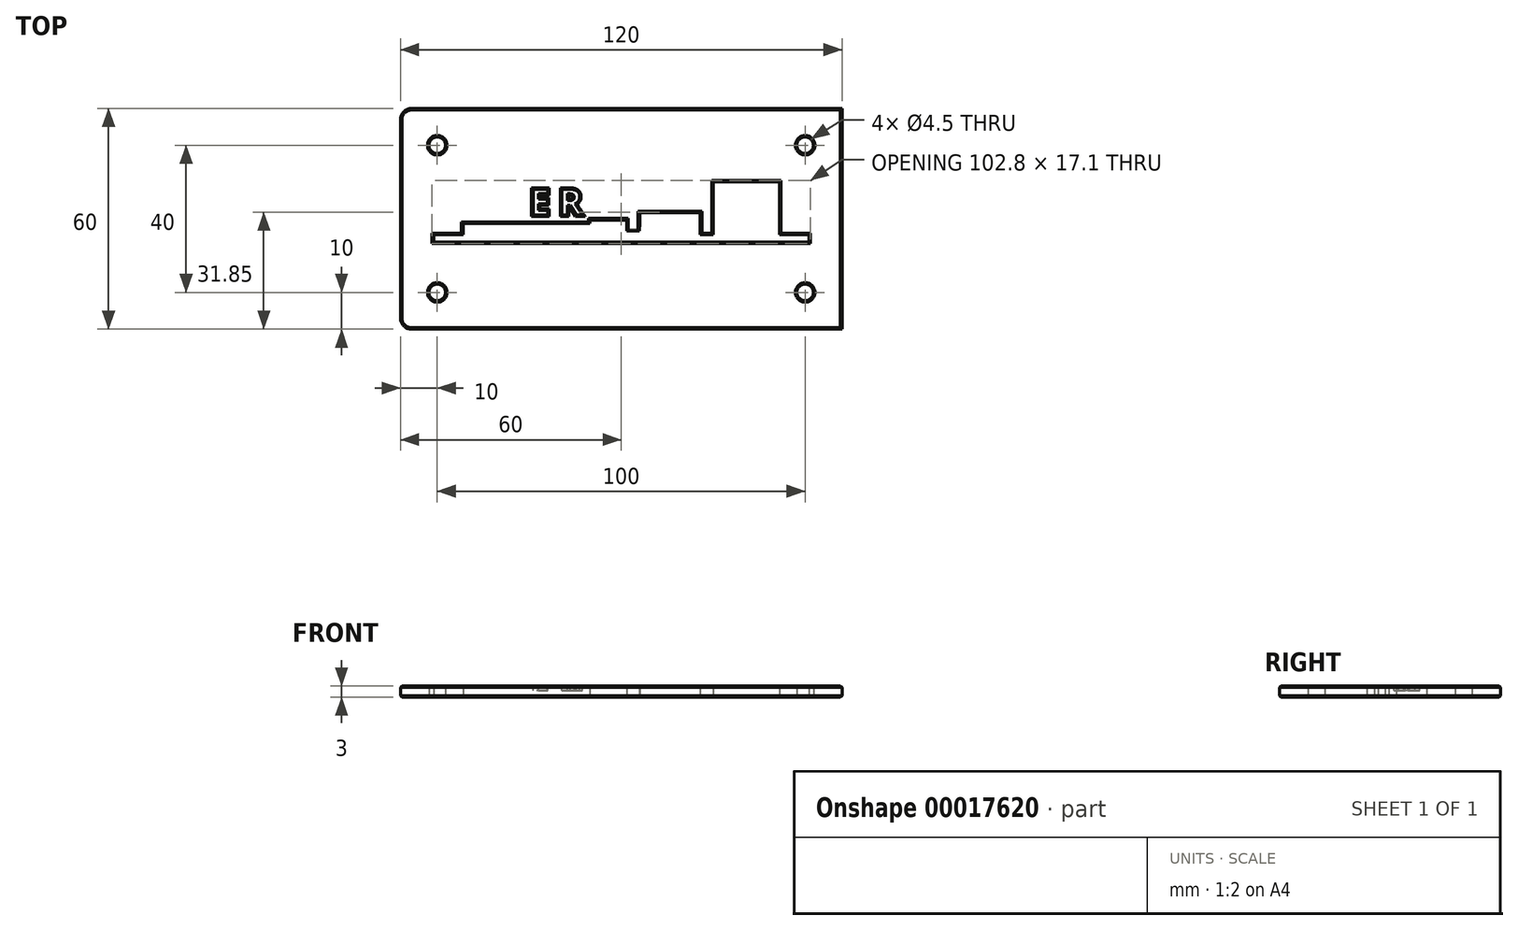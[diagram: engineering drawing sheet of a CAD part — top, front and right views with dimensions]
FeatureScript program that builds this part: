
annotation { "Feature Type Name" : "Feature", "Feature Type Description" : "" }
export const myFeature = defineFeature(function(context is Context, id is Id, definition is map)
    precondition{}
    {
        {
            var Q0;
            Q0=qCreatedBy(makeId("Top.planeOp"),FACE);
            var sketch = newSketch(context, id + "F0", { "sketchPlane" : qUnion([Q0])});
            skLineSegment(sketch, "E0.rect.bottom", {"start": v(-52.5, -30) * mm, "end": v(60, -30) * mm});
            skLineSegment(sketch, "E0.rect.top", {"start": v(-55, 30) * mm, "end": v(60, 30) * mm});
            skLineSegment(sketch, "E0.rect.left", {"start": v(-60, -22.5) * mm, "end": v(-60, 20) * mm});
            skLineSegment(sketch, "E0.rect.right", {"start": v(60, -30) * mm, "end": v(60, 30) * mm});
            skPoint(sketch, "E0.rect.middle", {"position": v(0, 0) * mm});
            skLineSegment(sketch, "E1.left", {"start": v(-60, -30) * mm, "end": v(-60, -22.5) * mm});
            skLineSegment(sketch, "E2.bottom", {"start": v(-60, 30) * mm, "end": v(-55, 30) * mm});
            skLineSegment(sketch, "E2.left", {"start": v(-60, 30) * mm, "end": v(-60, 20) * mm});
            skLineSegment(sketch, "E3.bottom", {"start": v(60, 30) * mm, "end": v(50, 30) * mm});
            skLineSegment(sketch, "E3.left", {"start": v(60, 30) * mm, "end": v(60, 22.5) * mm});
            skLineSegment(sketch, "E4.bottom", {"start": v(60, -30) * mm, "end": v(55, -30) * mm});
            skLineSegment(sketch, "E4.left", {"start": v(60, -30) * mm, "end": v(60, -22.5) * mm});
            skCircle(sketch, "E5", {"center": v(-50, -20) * mm, "radius": 2.25 * mm});
            skCircle(sketch, "E6", {"center": v(-50, 20) * mm, "radius": 2.25 * mm});
            skCircle(sketch, "E7", {"center": v(50, 20) * mm, "radius": 2.25 * mm});
            skCircle(sketch, "E8", {"center": v(50, -20) * mm, "radius": 2.25 * mm});
            skLineSegment(sketch, "E9", {"start": v(-51, 6.3) * mm, "end": v(1.5, 6.3) * mm});
            skLineSegment(sketch, "E10.top", {"start": v(-51, 4.3) * mm, "end": v(-43, 4.3) * mm});
            skLineSegment(sketch, "E10.left", {"start": v(-51, 6.3) * mm, "end": v(-51, 4.3) * mm});
            skLineSegment(sketch, "E10.right", {"start": v(51, 6.3) * mm, "end": v(51, 4.3) * mm});
            skLineSegment(sketch, "E11.top", {"start": v(-43, 1.3) * mm, "end": v(-8.5, 1.3) * mm});
            skLineSegment(sketch, "E11.left", {"start": v(-43, 4.3) * mm, "end": v(-43, 1.3) * mm});
            skLineSegment(sketch, "E11.right", {"start": v(43, 4.3) * mm, "end": v(43, 1.3) * mm});
            skLineSegment(sketch, "E12.trimOffspring", {"start": v(43, 4.3) * mm, "end": v(51, 4.3) * mm});
            skLineSegment(sketch, "E13.right", {"start": v(-8.5, 1.3) * mm, "end": v(-8.5, 0.3) * mm});
            skLineSegment(sketch, "E14.left", {"start": v(-8.5, 0.3) * mm, "end": v(-8.5, 1.3) * mm});
            skLineSegment(sketch, "E14.right", {"start": v(1.5, 0.3) * mm, "end": v(1.5, 1.3) * mm});
            skLineSegment(sketch, "E15.top", {"start": v(43, -10) * mm, "end": v(25, -10) * mm});
            skLineSegment(sketch, "E15.left", {"start": v(43, 1.3) * mm, "end": v(43, -10) * mm});
            skLineSegment(sketch, "E15.right", {"start": v(25, 1.3) * mm, "end": v(25, -10) * mm});
            skLineSegment(sketch, "E16.top", {"start": v(-8.5, 0.3) * mm, "end": v(1.5, 0.3) * mm});
            skLineSegment(sketch, "E16.right", {"start": v(1.5, 1.3) * mm, "end": v(1.5, 0.3) * mm});
            skLineSegment(sketch, "E17", {"start": v(-60, -30) * mm, "end": v(-52.5, -30) * mm});
            skLineSegment(sketch, "E18.left", {"start": v(25, 1.3) * mm, "end": v(25, 4.3) * mm});
            skLineSegment(sketch, "E18.right", {"start": v(21.5, 1.3) * mm, "end": v(21.5, 4.3) * mm});
            skLineSegment(sketch, "E19.left", {"start": v(1.5, 1.3) * mm, "end": v(1.5, 3.3) * mm});
            skLineSegment(sketch, "E20.top", {"start": v(5, -1.7) * mm, "end": v(21.5, -1.7) * mm});
            skLineSegment(sketch, "E20.left", {"start": v(5, 1.3) * mm, "end": v(5, -1.7) * mm});
            skLineSegment(sketch, "E20.right", {"start": v(21.5, 1.3) * mm, "end": v(21.5, -1.7) * mm});
            skLineSegment(sketch, "E21.trimOffspring", {"start": v(5, 6.3) * mm, "end": v(21.5, 6.3) * mm});
            skLineSegment(sketch, "E22.trimOffspring", {"start": v(25, 6.3) * mm, "end": v(51, 6.3) * mm});
            skLineSegment(sketch, "E23", {"start": v(-43, 4.3) * mm, "end": v(5, 4.3) * mm, "construction": true});
            skLineSegment(sketch, "E24", {"start": v(21.5, 4.3) * mm, "end": v(25, 4.3) * mm});
            skLineSegment(sketch, "E25", {"start": v(1.5, 6.3) * mm, "end": v(5, 6.3) * mm});
            skLineSegment(sketch, "E26", {"start": v(21.5, 6.3) * mm, "end": v(25, 6.3) * mm});
            skLineSegment(sketch, "E27", {"start": v(4.98, 3.3) * mm, "end": v(1.5, 3.3) * mm});
            skLineSegment(sketch, "E28.trimOffspring", {"start": v(21.5, 4.3) * mm, "end": v(43, 4.3) * mm, "construction": true});
            skLineSegment(sketch, "E29", {"start": v(4.98, 3.3) * mm, "end": v(5, 1.3) * mm});
            skLineSegment(sketch, "E30", {"start": v(21.5, 4.3) * mm, "end": v(5, 4.3) * mm, "construction": true});
            skSolve(sketch);
        }
        {
            var Q0;
            Q0=makeQuery(id+"F0.imprint","IMPRINT",FACE,{"disambiguationData":[TD([[makeQuery(id+"F0.imprint","IMPRINT",EDGE,{"derivedFrom":sQuery(id+"F0.wireOp",EDGE,"E0.rect.bottom")}),1.0]])]});
            extrude(context, id + "F1", {"entities" : qUnion([Q0]), "oppositeDirection" : true, "depth" : 3 * mm});
        }
        {
            var Q0;
            Q0=makeQuery(id+"F1.opExtrude","SWEPT_EDGE",EDGE,{"disambiguationData":[OSD([sQuery(id+"F0.wireOp",EDGE,"E4.bottom"),sQuery(id+"F0.wireOp",EDGE,"E4.left")])]});
            var Q1;
            Q1=makeQuery(id+"F1.opExtrude","SWEPT_EDGE",EDGE,{"disambiguationData":[OSD([sQuery(id+"F0.wireOp",EDGE,"E1.bottom"),sQuery(id+"F0.wireOp",EDGE,"E1.left")])]});
            var Q2;
            Q2=makeQuery(id+"F1.opExtrude","SWEPT_EDGE",EDGE,{"disambiguationData":[OSD([sQuery(id+"F0.wireOp",EDGE,"E3.bottom"),sQuery(id+"F0.wireOp",EDGE,"E3.left")])]});
            var Q3;
            Q3=makeQuery(id+"F1.opExtrude","SWEPT_EDGE",EDGE,{"disambiguationData":[OSD([sQuery(id+"F0.wireOp",EDGE,"E2.bottom"),sQuery(id+"F0.wireOp",EDGE,"E2.left")])]});
            fillet(context, id + "F2", {"entities" : qUnion([Q0, Q1, Q2, Q3]), "radius" : 3 * mm, "tangentPropagation" : true, "allowEdgeOverflow" : false});
        }
        {
            var Q0;
            Q0=makeQuery(id+"F1.opExtrude","CAP_FACE",FACE,{"disambiguationData":[OSD([sQuery(id+"F0.wireOp",EDGE,"E0.rect.bottom"),sQuery(id+"F0.wireOp",EDGE,"E0.rect.top"),sQuery(id+"F0.wireOp",EDGE,"E0.rect.left"),sQuery(id+"F0.wireOp",EDGE,"E0.rect.right"),sQuery(id+"F0.wireOp",EDGE,"E1.bottom"),sQuery(id+"F0.wireOp",EDGE,"E1.left"),sQuery(id+"F0.wireOp",EDGE,"E2.bottom"),sQuery(id+"F0.wireOp",EDGE,"E2.left"),sQuery(id+"F0.wireOp",EDGE,"E3.bottom"),sQuery(id+"F0.wireOp",EDGE,"E3.left"),sQuery(id+"F0.wireOp",EDGE,"E4.bottom"),sQuery(id+"F0.wireOp",EDGE,"E4.left"),sQuery(id+"F0.wireOp",EDGE,"E5"),sQuery(id+"F0.wireOp",EDGE,"E6"),sQuery(id+"F0.wireOp",EDGE,"E7"),sQuery(id+"F0.wireOp",EDGE,"E8"),sQuery(id+"F0.wireOp",EDGE,"E9"),sQuery(id+"F0.wireOp",EDGE,"E10.top"),sQuery(id+"F0.wireOp",EDGE,"E10.left"),sQuery(id+"F0.wireOp",EDGE,"E10.right"),sQuery(id+"F0.wireOp",EDGE,"E11.left"),sQuery(id+"F0.wireOp",EDGE,"E11.right"),sQuery(id+"F0.wireOp",EDGE,"E12.trimOffspring"),sQuery(id+"F0.wireOp",EDGE,"E11.top"),sQuery(id+"F0.wireOp",EDGE,"E14.bottom"),sQuery(id+"F0.wireOp",EDGE,"E14.left"),sQuery(id+"F0.wireOp",EDGE,"E14.right"),sQuery(id+"F0.wireOp",EDGE,"2bbd994b-3e8e-4b0d-a158-f2154df3f7ed.trimOffspring"),sQuery(id+"F0.wireOp",EDGE,"E15.top"),sQuery(id+"F0.wireOp",EDGE,"E15.left"),sQuery(id+"F0.wireOp",EDGE,"E15.right")])],"isStart":false});
            var sketch = newSketch(context, id + "F3", { "sketchPlane" : qUnion([Q0])});
            skText(sketch, "E31", { "text": "E", "fontName": "OpenSans-Bold.ttf"});
            skText(sketch, "E32", { "text": "R", "fontName": "OpenSans-Bold.ttf"});
            skPoint(sketch, "E33.right.start.orphan", {"position": v(-26.9, 1.1) * mm});
            skPoint(sketch, "E34.orphan", {"position": v(-8.9, -0.9) * mm});
            skPoint(sketch, "E33.bottom.end.orphan", {"position": v(-26.9, -0.9) * mm});
            skPoint(sketch, "E33.bottom.start.orphan", {"position": v(-17.9, -0.9) * mm});
            skLineSegment(sketch, "E35", {"start": v(-43, -1.3) * mm, "end": v(-8.5, -1.3) * mm});
            const initialGuessF3  = {"E31": [-0.02483, 0.0011, 1, 0, 0.007], "E32": [-0.01696, 0.0011, 1, 0, 0.007]};
            skSetInitialGuess(sketch, initialGuessF3);
            skSolve(sketch);
        }
        {
            var Q0;
            Q0=makeQuery(id+"F3.imprint","IMPRINT",FACE,{"disambiguationData":[TD([[makeQuery(id+"F3.imprint","IMPRINT",EDGE,{"derivedFrom":sQuery(id+"F3.wireOp",EDGE,"E31.sketch_text.stroke-0")}),-1.0]])]});
            var Q1;
            Q1=makeQuery(id+"F3.imprint","IMPRINT",FACE,{"disambiguationData":[TD([[makeQuery(id+"F3.imprint","IMPRINT",EDGE,{"derivedFrom":sQuery(id+"F3.wireOp",EDGE,"E32.sketch_text.stroke-0")}),-1.0]])]});
            extrude(context, id + "F4", {"entities" : qUnion([Q0, Q1]), "operationType" : NewBodyOperationType.REMOVE, "oppositeDirection" : true, "depth" : 1.2 * mm});
        }
        {
            var Q0;
            Q0=makeQuery(id+"F4.boolean.opBoolean","COPY",EDGE,{"derivedFrom":makeQuery(id+"F4.opExtrude","CAP_EDGE",EDGE,{"disambiguationData":[OSD([sQuery(id+"F3.wireOp",EDGE,"E31.sketch_text.stroke-1")])],"isStart":true})});
            var Q1;
            Q1=makeQuery(id+"F4.boolean.opBoolean","COPY",EDGE,{"derivedFrom":makeQuery(id+"F4.opExtrude","CAP_EDGE",EDGE,{"disambiguationData":[OSD([sQuery(id+"F3.wireOp",EDGE,"E31.sketch_text.stroke-2")])],"isStart":true})});
            var Q2;
            Q2=makeQuery(id+"F4.boolean.opBoolean","COPY",EDGE,{"derivedFrom":makeQuery(id+"F4.opExtrude","CAP_EDGE",EDGE,{"disambiguationData":[OSD([sQuery(id+"F3.wireOp",EDGE,"E31.sketch_text.stroke-3")])],"isStart":true})});
            var Q3;
            Q3=makeQuery(id+"F4.boolean.opBoolean","COPY",EDGE,{"derivedFrom":makeQuery(id+"F4.opExtrude","CAP_EDGE",EDGE,{"disambiguationData":[OSD([sQuery(id+"F3.wireOp",EDGE,"E31.sketch_text.stroke-4")])],"isStart":true})});
            var Q4;
            Q4=makeQuery(id+"F4.boolean.opBoolean","COPY",EDGE,{"derivedFrom":makeQuery(id+"F4.opExtrude","CAP_EDGE",EDGE,{"disambiguationData":[OSD([sQuery(id+"F3.wireOp",EDGE,"E31.sketch_text.stroke-5")])],"isStart":true})});
            var Q5;
            Q5=makeQuery(id+"F4.boolean.opBoolean","COPY",EDGE,{"derivedFrom":makeQuery(id+"F4.opExtrude","CAP_EDGE",EDGE,{"disambiguationData":[OSD([sQuery(id+"F3.wireOp",EDGE,"E31.sketch_text.stroke-6")])],"isStart":true})});
            var Q6;
            Q6=makeQuery(id+"F4.boolean.opBoolean","COPY",EDGE,{"derivedFrom":makeQuery(id+"F4.opExtrude","CAP_EDGE",EDGE,{"disambiguationData":[OSD([sQuery(id+"F3.wireOp",EDGE,"E31.sketch_text.stroke-7")])],"isStart":true})});
            var Q7;
            Q7=makeQuery(id+"F4.boolean.opBoolean","COPY",EDGE,{"derivedFrom":makeQuery(id+"F4.opExtrude","CAP_EDGE",EDGE,{"disambiguationData":[OSD([sQuery(id+"F3.wireOp",EDGE,"E31.sketch_text.stroke-8")])],"isStart":true})});
            var Q8;
            Q8=makeQuery(id+"F4.boolean.opBoolean","COPY",EDGE,{"derivedFrom":makeQuery(id+"F4.opExtrude","CAP_EDGE",EDGE,{"disambiguationData":[OSD([sQuery(id+"F3.wireOp",EDGE,"E31.sketch_text.stroke-9")])],"isStart":true})});
            var Q9;
            Q9=makeQuery(id+"F4.boolean.opBoolean","COPY",EDGE,{"derivedFrom":makeQuery(id+"F4.opExtrude","CAP_EDGE",EDGE,{"disambiguationData":[OSD([sQuery(id+"F3.wireOp",EDGE,"E31.sketch_text.stroke-10")])],"isStart":true})});
            var Q10;
            Q10=makeQuery(id+"F4.boolean.opBoolean","COPY",EDGE,{"derivedFrom":makeQuery(id+"F4.opExtrude","CAP_EDGE",EDGE,{"disambiguationData":[OSD([sQuery(id+"F3.wireOp",EDGE,"E31.sketch_text.stroke-11")])],"isStart":true})});
            var Q11;
            Q11=makeQuery(id+"F4.boolean.opBoolean","COPY",EDGE,{"derivedFrom":makeQuery(id+"F4.opExtrude","CAP_EDGE",EDGE,{"disambiguationData":[OSD([sQuery(id+"F3.wireOp",EDGE,"E31.sketch_text.stroke-0")])],"isStart":true})});
            var Q12;
            Q12=makeQuery(id+"F4.boolean.opBoolean","COPY",EDGE,{"derivedFrom":makeQuery(id+"F4.opExtrude","CAP_EDGE",EDGE,{"disambiguationData":[OSD([sQuery(id+"F3.wireOp",EDGE,"E32.sketch_text.stroke-9")])],"isStart":true})});
            var Q13;
            Q13=makeQuery(id+"F4.boolean.opBoolean","COPY",EDGE,{"derivedFrom":makeQuery(id+"F4.opExtrude","CAP_EDGE",EDGE,{"disambiguationData":[OSD([sQuery(id+"F3.wireOp",EDGE,"E32.sketch_text.stroke-8")])],"isStart":true})});
            var Q14;
            Q14=makeQuery(id+"F4.boolean.opBoolean","COPY",EDGE,{"derivedFrom":makeQuery(id+"F4.opExtrude","CAP_EDGE",EDGE,{"disambiguationData":[OSD([sQuery(id+"F3.wireOp",EDGE,"E32.sketch_text.stroke-7")])],"isStart":true})});
            var Q15;
            Q15=makeQuery(id+"F4.boolean.opBoolean","COPY",EDGE,{"derivedFrom":makeQuery(id+"F4.opExtrude","CAP_EDGE",EDGE,{"disambiguationData":[OSD([sQuery(id+"F3.wireOp",EDGE,"E32.sketch_text.stroke-18")])],"isStart":true})});
            var Q16;
            Q16=makeQuery(id+"F4.boolean.opBoolean","COPY",EDGE,{"derivedFrom":makeQuery(id+"F4.opExtrude","CAP_EDGE",EDGE,{"disambiguationData":[OSD([sQuery(id+"F3.wireOp",EDGE,"E32.sketch_text.stroke-17")])],"isStart":true})});
            var Q17;
            Q17=makeQuery(id+"F4.boolean.opBoolean","COPY",EDGE,{"derivedFrom":makeQuery(id+"F4.opExtrude","CAP_EDGE",EDGE,{"disambiguationData":[OSD([sQuery(id+"F3.wireOp",EDGE,"E32.sketch_text.stroke-16")])],"isStart":true})});
            var Q18;
            Q18=makeQuery(id+"F4.boolean.opBoolean","COPY",EDGE,{"derivedFrom":makeQuery(id+"F4.opExtrude","CAP_EDGE",EDGE,{"disambiguationData":[OSD([sQuery(id+"F3.wireOp",EDGE,"E32.sketch_text.stroke-15")])],"isStart":true})});
            var Q19;
            Q19=makeQuery(id+"F4.boolean.opBoolean","COPY",EDGE,{"derivedFrom":makeQuery(id+"F4.opExtrude","CAP_EDGE",EDGE,{"disambiguationData":[OSD([sQuery(id+"F3.wireOp",EDGE,"E32.sketch_text.stroke-14")])],"isStart":true})});
            var Q20;
            Q20=makeQuery(id+"F4.boolean.opBoolean","COPY",EDGE,{"derivedFrom":makeQuery(id+"F4.opExtrude","CAP_EDGE",EDGE,{"disambiguationData":[OSD([sQuery(id+"F3.wireOp",EDGE,"E32.sketch_text.stroke-13")])],"isStart":true})});
            var Q21;
            Q21=makeQuery(id+"F4.boolean.opBoolean","COPY",EDGE,{"derivedFrom":makeQuery(id+"F4.opExtrude","CAP_EDGE",EDGE,{"disambiguationData":[OSD([sQuery(id+"F3.wireOp",EDGE,"E32.sketch_text.stroke-12")])],"isStart":true})});
            var Q22;
            Q22=makeQuery(id+"F4.boolean.opBoolean","COPY",EDGE,{"derivedFrom":makeQuery(id+"F4.opExtrude","CAP_EDGE",EDGE,{"disambiguationData":[OSD([sQuery(id+"F3.wireOp",EDGE,"E32.sketch_text.stroke-11")])],"isStart":true})});
            var Q23;
            Q23=makeQuery(id+"F4.boolean.opBoolean","COPY",EDGE,{"derivedFrom":makeQuery(id+"F4.opExtrude","CAP_EDGE",EDGE,{"disambiguationData":[OSD([sQuery(id+"F3.wireOp",EDGE,"E32.sketch_text.stroke-10")])],"isStart":true})});
            var Q24;
            Q24=makeQuery(id+"F4.boolean.opBoolean","SPLIT",FACE,{"disambiguationData":[TD([makeQuery(id+"F4.opExtrude","SWEPT_FACE",FACE,{"disambiguationData":[OSD([sQuery(id+"F3.wireOp",EDGE,"E32.sketch_text.stroke-0")])]})])],"derivedFrom":makeQuery(id+"F1.opExtrude","CAP_FACE",FACE,{"disambiguationData":[OSD([sQuery(id+"F0.wireOp",EDGE,"E0.rect.bottom"),sQuery(id+"F0.wireOp",EDGE,"E0.rect.top"),sQuery(id+"F0.wireOp",EDGE,"E0.rect.left"),sQuery(id+"F0.wireOp",EDGE,"E0.rect.right"),sQuery(id+"F0.wireOp",EDGE,"E1.left"),sQuery(id+"F0.wireOp",EDGE,"E2.bottom"),sQuery(id+"F0.wireOp",EDGE,"E2.left"),sQuery(id+"F0.wireOp",EDGE,"E3.bottom"),sQuery(id+"F0.wireOp",EDGE,"E3.left"),sQuery(id+"F0.wireOp",EDGE,"E4.bottom"),sQuery(id+"F0.wireOp",EDGE,"E4.left"),sQuery(id+"F0.wireOp",EDGE,"E5"),sQuery(id+"F0.wireOp",EDGE,"E6"),sQuery(id+"F0.wireOp",EDGE,"E7"),sQuery(id+"F0.wireOp",EDGE,"E8"),sQuery(id+"F0.wireOp",EDGE,"E9"),sQuery(id+"F0.wireOp",EDGE,"E10.top"),sQuery(id+"F0.wireOp",EDGE,"E10.left"),sQuery(id+"F0.wireOp",EDGE,"E10.right"),sQuery(id+"F0.wireOp",EDGE,"E11.left"),sQuery(id+"F0.wireOp",EDGE,"E11.right"),sQuery(id+"F0.wireOp",EDGE,"E12.trimOffspring"),sQuery(id+"F0.wireOp",EDGE,"E11.top"),sQuery(id+"F0.wireOp",EDGE,"E15.top"),sQuery(id+"F0.wireOp",EDGE,"E15.left"),sQuery(id+"F0.wireOp",EDGE,"E15.right"),sQuery(id+"F0.wireOp",EDGE,"E16.top"),sQuery(id+"F0.wireOp",EDGE,"E13.right"),sQuery(id+"F0.wireOp",EDGE,"E16.right"),sQuery(id+"F0.wireOp",EDGE,"E17"),sQuery(id+"F0.wireOp",EDGE,"E18.left"),sQuery(id+"F0.wireOp",EDGE,"E18.right"),sQuery(id+"F0.wireOp",EDGE,"E19.left"),sQuery(id+"F0.wireOp",EDGE,"E19.right"),sQuery(id+"F0.wireOp",EDGE,"E20.top"),sQuery(id+"F0.wireOp",EDGE,"E20.left"),sQuery(id+"F0.wireOp",EDGE,"E20.right"),sQuery(id+"F0.wireOp",EDGE,"E21.trimOffspring"),sQuery(id+"F0.wireOp",EDGE,"E22.trimOffspring"),sQuery(id+"F0.wireOp",EDGE,"54661143-fa5e-42c1-9d10-70f3552f3fbd"),sQuery(id+"F0.wireOp",EDGE,"E24"),sQuery(id+"F0.wireOp",EDGE,"E25"),sQuery(id+"F0.wireOp",EDGE,"E26")])],"isStart":false})});
            chamfer(context, id + "F5", {"entities" : qUnion([Q0, Q1, Q2, Q3, Q4, Q5, Q6, Q7, Q8, Q9, Q10, Q11, Q12, Q13, Q14, Q15, Q16, Q17, Q18, Q19, Q20, Q21, Q22, Q23, Q24]), "width" : .4 * mm});
        }
        {
            var Q0;
            Q0=makeQuery(id+"F1.opExtrude","CAP_EDGE",EDGE,{"disambiguationData":[OSD([sQuery(id+"F0.wireOp",EDGE,"E0.rect.bottom"),sQuery(id+"F0.wireOp",EDGE,"E4.bottom"),sQuery(id+"F0.wireOp",EDGE,"E17")])],"isStart":false});
            var Q1;
            {var subQ0=sQuery(id+"F0.wireOp",EDGE,"E1.left");var subQ1=sQuery(id+"F0.wireOp",EDGE,"E17");Q1=makeQuery(id+"F2.opFillet","BLEND_EDGE",EDGE,{"blendedFrom":[makeQuery(id+"F1.opExtrude","SWEPT_EDGE",EDGE,{"disambiguationData":[OSD([subQ0,subQ1])]}),makeQuery(id+"F1.opExtrude","CAP_FACE",FACE,{"disambiguationData":[OSD([sQuery(id+"F0.wireOp",EDGE,"E0.rect.bottom"),sQuery(id+"F0.wireOp",EDGE,"E0.rect.top"),sQuery(id+"F0.wireOp",EDGE,"E0.rect.left"),sQuery(id+"F0.wireOp",EDGE,"E0.rect.right"),subQ0,sQuery(id+"F0.wireOp",EDGE,"E2.bottom"),sQuery(id+"F0.wireOp",EDGE,"E2.left"),sQuery(id+"F0.wireOp",EDGE,"E3.bottom"),sQuery(id+"F0.wireOp",EDGE,"E3.left"),sQuery(id+"F0.wireOp",EDGE,"E4.bottom"),sQuery(id+"F0.wireOp",EDGE,"E4.left"),sQuery(id+"F0.wireOp",EDGE,"E5"),sQuery(id+"F0.wireOp",EDGE,"E6"),sQuery(id+"F0.wireOp",EDGE,"E7"),sQuery(id+"F0.wireOp",EDGE,"E8"),sQuery(id+"F0.wireOp",EDGE,"E9"),sQuery(id+"F0.wireOp",EDGE,"E10.top"),sQuery(id+"F0.wireOp",EDGE,"E10.left"),sQuery(id+"F0.wireOp",EDGE,"E10.right"),sQuery(id+"F0.wireOp",EDGE,"E11.left"),sQuery(id+"F0.wireOp",EDGE,"E11.right"),sQuery(id+"F0.wireOp",EDGE,"E12.trimOffspring"),sQuery(id+"F0.wireOp",EDGE,"E11.top"),sQuery(id+"F0.wireOp",EDGE,"E15.top"),sQuery(id+"F0.wireOp",EDGE,"E15.left"),sQuery(id+"F0.wireOp",EDGE,"E15.right"),sQuery(id+"F0.wireOp",EDGE,"E16.top"),sQuery(id+"F0.wireOp",EDGE,"E13.right"),sQuery(id+"F0.wireOp",EDGE,"E16.right"),subQ1,sQuery(id+"F0.wireOp",EDGE,"E18.left"),sQuery(id+"F0.wireOp",EDGE,"E18.right"),sQuery(id+"F0.wireOp",EDGE,"E19.left"),sQuery(id+"F0.wireOp",EDGE,"E19.right"),sQuery(id+"F0.wireOp",EDGE,"E20.top"),sQuery(id+"F0.wireOp",EDGE,"E20.left"),sQuery(id+"F0.wireOp",EDGE,"E20.right"),sQuery(id+"F0.wireOp",EDGE,"E21.trimOffspring"),sQuery(id+"F0.wireOp",EDGE,"E22.trimOffspring"),sQuery(id+"F0.wireOp",EDGE,"54661143-fa5e-42c1-9d10-70f3552f3fbd"),sQuery(id+"F0.wireOp",EDGE,"E24"),sQuery(id+"F0.wireOp",EDGE,"E25"),sQuery(id+"F0.wireOp",EDGE,"E26")])],"isStart":false})],"blendedInto":[makeQuery(id+"F1.opExtrude","CAP_FACE",FACE,{"disambiguationData":[OSD([sQuery(id+"F0.wireOp",EDGE,"E0.rect.bottom"),sQuery(id+"F0.wireOp",EDGE,"E0.rect.top"),sQuery(id+"F0.wireOp",EDGE,"E0.rect.left"),sQuery(id+"F0.wireOp",EDGE,"E0.rect.right"),subQ0,sQuery(id+"F0.wireOp",EDGE,"E2.bottom"),sQuery(id+"F0.wireOp",EDGE,"E2.left"),sQuery(id+"F0.wireOp",EDGE,"E3.bottom"),sQuery(id+"F0.wireOp",EDGE,"E3.left"),sQuery(id+"F0.wireOp",EDGE,"E4.bottom"),sQuery(id+"F0.wireOp",EDGE,"E4.left"),sQuery(id+"F0.wireOp",EDGE,"E5"),sQuery(id+"F0.wireOp",EDGE,"E6"),sQuery(id+"F0.wireOp",EDGE,"E7"),sQuery(id+"F0.wireOp",EDGE,"E8"),sQuery(id+"F0.wireOp",EDGE,"E9"),sQuery(id+"F0.wireOp",EDGE,"E10.top"),sQuery(id+"F0.wireOp",EDGE,"E10.left"),sQuery(id+"F0.wireOp",EDGE,"E10.right"),sQuery(id+"F0.wireOp",EDGE,"E11.left"),sQuery(id+"F0.wireOp",EDGE,"E11.right"),sQuery(id+"F0.wireOp",EDGE,"E12.trimOffspring"),sQuery(id+"F0.wireOp",EDGE,"E11.top"),sQuery(id+"F0.wireOp",EDGE,"E15.top"),sQuery(id+"F0.wireOp",EDGE,"E15.left"),sQuery(id+"F0.wireOp",EDGE,"E15.right"),sQuery(id+"F0.wireOp",EDGE,"E16.top"),sQuery(id+"F0.wireOp",EDGE,"E13.right"),sQuery(id+"F0.wireOp",EDGE,"E16.right"),subQ1,sQuery(id+"F0.wireOp",EDGE,"E18.left"),sQuery(id+"F0.wireOp",EDGE,"E18.right"),sQuery(id+"F0.wireOp",EDGE,"E19.left"),sQuery(id+"F0.wireOp",EDGE,"E19.right"),sQuery(id+"F0.wireOp",EDGE,"E20.top"),sQuery(id+"F0.wireOp",EDGE,"E20.left"),sQuery(id+"F0.wireOp",EDGE,"E20.right"),sQuery(id+"F0.wireOp",EDGE,"E21.trimOffspring"),sQuery(id+"F0.wireOp",EDGE,"E22.trimOffspring"),sQuery(id+"F0.wireOp",EDGE,"54661143-fa5e-42c1-9d10-70f3552f3fbd"),sQuery(id+"F0.wireOp",EDGE,"E24"),sQuery(id+"F0.wireOp",EDGE,"E25"),sQuery(id+"F0.wireOp",EDGE,"E26")])],"isStart":false})]});}
            var Q2;
            Q2=makeQuery(id+"F1.opExtrude","CAP_EDGE",EDGE,{"disambiguationData":[OSD([sQuery(id+"F0.wireOp",EDGE,"E0.rect.left"),sQuery(id+"F0.wireOp",EDGE,"E1.left"),sQuery(id+"F0.wireOp",EDGE,"E2.left")])],"isStart":false});
            var Q3;
            {var subQ0=sQuery(id+"F0.wireOp",EDGE,"E4.bottom");var subQ1=sQuery(id+"F0.wireOp",EDGE,"E4.left");Q3=makeQuery(id+"F2.opFillet","BLEND_EDGE",EDGE,{"blendedFrom":[makeQuery(id+"F1.opExtrude","SWEPT_EDGE",EDGE,{"disambiguationData":[OSD([subQ0,subQ1])]}),makeQuery(id+"F1.opExtrude","CAP_FACE",FACE,{"disambiguationData":[OSD([sQuery(id+"F0.wireOp",EDGE,"E0.rect.bottom"),sQuery(id+"F0.wireOp",EDGE,"E0.rect.top"),sQuery(id+"F0.wireOp",EDGE,"E0.rect.left"),sQuery(id+"F0.wireOp",EDGE,"E0.rect.right"),sQuery(id+"F0.wireOp",EDGE,"E1.left"),sQuery(id+"F0.wireOp",EDGE,"E2.bottom"),sQuery(id+"F0.wireOp",EDGE,"E2.left"),sQuery(id+"F0.wireOp",EDGE,"E3.bottom"),sQuery(id+"F0.wireOp",EDGE,"E3.left"),subQ0,subQ1,sQuery(id+"F0.wireOp",EDGE,"E5"),sQuery(id+"F0.wireOp",EDGE,"E6"),sQuery(id+"F0.wireOp",EDGE,"E7"),sQuery(id+"F0.wireOp",EDGE,"E8"),sQuery(id+"F0.wireOp",EDGE,"E9"),sQuery(id+"F0.wireOp",EDGE,"E10.top"),sQuery(id+"F0.wireOp",EDGE,"E10.left"),sQuery(id+"F0.wireOp",EDGE,"E10.right"),sQuery(id+"F0.wireOp",EDGE,"E11.left"),sQuery(id+"F0.wireOp",EDGE,"E11.right"),sQuery(id+"F0.wireOp",EDGE,"E12.trimOffspring"),sQuery(id+"F0.wireOp",EDGE,"E11.top"),sQuery(id+"F0.wireOp",EDGE,"E15.top"),sQuery(id+"F0.wireOp",EDGE,"E15.left"),sQuery(id+"F0.wireOp",EDGE,"E15.right"),sQuery(id+"F0.wireOp",EDGE,"E16.top"),sQuery(id+"F0.wireOp",EDGE,"E13.right"),sQuery(id+"F0.wireOp",EDGE,"E16.right"),sQuery(id+"F0.wireOp",EDGE,"E17"),sQuery(id+"F0.wireOp",EDGE,"E18.left"),sQuery(id+"F0.wireOp",EDGE,"E18.right"),sQuery(id+"F0.wireOp",EDGE,"E19.left"),sQuery(id+"F0.wireOp",EDGE,"E19.right"),sQuery(id+"F0.wireOp",EDGE,"E20.top"),sQuery(id+"F0.wireOp",EDGE,"E20.left"),sQuery(id+"F0.wireOp",EDGE,"E20.right"),sQuery(id+"F0.wireOp",EDGE,"E21.trimOffspring"),sQuery(id+"F0.wireOp",EDGE,"E22.trimOffspring"),sQuery(id+"F0.wireOp",EDGE,"54661143-fa5e-42c1-9d10-70f3552f3fbd"),sQuery(id+"F0.wireOp",EDGE,"E24"),sQuery(id+"F0.wireOp",EDGE,"E25"),sQuery(id+"F0.wireOp",EDGE,"E26")])],"isStart":false})],"blendedInto":[makeQuery(id+"F1.opExtrude","CAP_FACE",FACE,{"disambiguationData":[OSD([sQuery(id+"F0.wireOp",EDGE,"E0.rect.bottom"),sQuery(id+"F0.wireOp",EDGE,"E0.rect.top"),sQuery(id+"F0.wireOp",EDGE,"E0.rect.left"),sQuery(id+"F0.wireOp",EDGE,"E0.rect.right"),sQuery(id+"F0.wireOp",EDGE,"E1.left"),sQuery(id+"F0.wireOp",EDGE,"E2.bottom"),sQuery(id+"F0.wireOp",EDGE,"E2.left"),sQuery(id+"F0.wireOp",EDGE,"E3.bottom"),sQuery(id+"F0.wireOp",EDGE,"E3.left"),subQ0,subQ1,sQuery(id+"F0.wireOp",EDGE,"E5"),sQuery(id+"F0.wireOp",EDGE,"E6"),sQuery(id+"F0.wireOp",EDGE,"E7"),sQuery(id+"F0.wireOp",EDGE,"E8"),sQuery(id+"F0.wireOp",EDGE,"E9"),sQuery(id+"F0.wireOp",EDGE,"E10.top"),sQuery(id+"F0.wireOp",EDGE,"E10.left"),sQuery(id+"F0.wireOp",EDGE,"E10.right"),sQuery(id+"F0.wireOp",EDGE,"E11.left"),sQuery(id+"F0.wireOp",EDGE,"E11.right"),sQuery(id+"F0.wireOp",EDGE,"E12.trimOffspring"),sQuery(id+"F0.wireOp",EDGE,"E11.top"),sQuery(id+"F0.wireOp",EDGE,"E15.top"),sQuery(id+"F0.wireOp",EDGE,"E15.left"),sQuery(id+"F0.wireOp",EDGE,"E15.right"),sQuery(id+"F0.wireOp",EDGE,"E16.top"),sQuery(id+"F0.wireOp",EDGE,"E13.right"),sQuery(id+"F0.wireOp",EDGE,"E16.right"),sQuery(id+"F0.wireOp",EDGE,"E17"),sQuery(id+"F0.wireOp",EDGE,"E18.left"),sQuery(id+"F0.wireOp",EDGE,"E18.right"),sQuery(id+"F0.wireOp",EDGE,"E19.left"),sQuery(id+"F0.wireOp",EDGE,"E19.right"),sQuery(id+"F0.wireOp",EDGE,"E20.top"),sQuery(id+"F0.wireOp",EDGE,"E20.left"),sQuery(id+"F0.wireOp",EDGE,"E20.right"),sQuery(id+"F0.wireOp",EDGE,"E21.trimOffspring"),sQuery(id+"F0.wireOp",EDGE,"E22.trimOffspring"),sQuery(id+"F0.wireOp",EDGE,"54661143-fa5e-42c1-9d10-70f3552f3fbd"),sQuery(id+"F0.wireOp",EDGE,"E24"),sQuery(id+"F0.wireOp",EDGE,"E25"),sQuery(id+"F0.wireOp",EDGE,"E26")])],"isStart":false})]});}
            var Q4;
            Q4=makeQuery(id+"F1.opExtrude","CAP_EDGE",EDGE,{"disambiguationData":[OSD([sQuery(id+"F0.wireOp",EDGE,"E0.rect.right"),sQuery(id+"F0.wireOp",EDGE,"E3.left"),sQuery(id+"F0.wireOp",EDGE,"E4.left")])],"isStart":false});
            var Q5;
            {var subQ0=sQuery(id+"F0.wireOp",EDGE,"E3.bottom");var subQ1=sQuery(id+"F0.wireOp",EDGE,"E3.left");Q5=makeQuery(id+"F2.opFillet","BLEND_EDGE",EDGE,{"blendedFrom":[makeQuery(id+"F1.opExtrude","SWEPT_EDGE",EDGE,{"disambiguationData":[OSD([subQ0,subQ1])]}),makeQuery(id+"F1.opExtrude","CAP_FACE",FACE,{"disambiguationData":[OSD([sQuery(id+"F0.wireOp",EDGE,"E0.rect.bottom"),sQuery(id+"F0.wireOp",EDGE,"E0.rect.top"),sQuery(id+"F0.wireOp",EDGE,"E0.rect.left"),sQuery(id+"F0.wireOp",EDGE,"E0.rect.right"),sQuery(id+"F0.wireOp",EDGE,"E1.left"),sQuery(id+"F0.wireOp",EDGE,"E2.bottom"),sQuery(id+"F0.wireOp",EDGE,"E2.left"),subQ0,subQ1,sQuery(id+"F0.wireOp",EDGE,"E4.bottom"),sQuery(id+"F0.wireOp",EDGE,"E4.left"),sQuery(id+"F0.wireOp",EDGE,"E5"),sQuery(id+"F0.wireOp",EDGE,"E6"),sQuery(id+"F0.wireOp",EDGE,"E7"),sQuery(id+"F0.wireOp",EDGE,"E8"),sQuery(id+"F0.wireOp",EDGE,"E9"),sQuery(id+"F0.wireOp",EDGE,"E10.top"),sQuery(id+"F0.wireOp",EDGE,"E10.left"),sQuery(id+"F0.wireOp",EDGE,"E10.right"),sQuery(id+"F0.wireOp",EDGE,"E11.left"),sQuery(id+"F0.wireOp",EDGE,"E11.right"),sQuery(id+"F0.wireOp",EDGE,"E12.trimOffspring"),sQuery(id+"F0.wireOp",EDGE,"E11.top"),sQuery(id+"F0.wireOp",EDGE,"E15.top"),sQuery(id+"F0.wireOp",EDGE,"E15.left"),sQuery(id+"F0.wireOp",EDGE,"E15.right"),sQuery(id+"F0.wireOp",EDGE,"E16.top"),sQuery(id+"F0.wireOp",EDGE,"E13.right"),sQuery(id+"F0.wireOp",EDGE,"E16.right"),sQuery(id+"F0.wireOp",EDGE,"E17"),sQuery(id+"F0.wireOp",EDGE,"E18.left"),sQuery(id+"F0.wireOp",EDGE,"E18.right"),sQuery(id+"F0.wireOp",EDGE,"E19.left"),sQuery(id+"F0.wireOp",EDGE,"E19.right"),sQuery(id+"F0.wireOp",EDGE,"E20.top"),sQuery(id+"F0.wireOp",EDGE,"E20.left"),sQuery(id+"F0.wireOp",EDGE,"E20.right"),sQuery(id+"F0.wireOp",EDGE,"E21.trimOffspring"),sQuery(id+"F0.wireOp",EDGE,"E22.trimOffspring"),sQuery(id+"F0.wireOp",EDGE,"54661143-fa5e-42c1-9d10-70f3552f3fbd"),sQuery(id+"F0.wireOp",EDGE,"E24"),sQuery(id+"F0.wireOp",EDGE,"E25"),sQuery(id+"F0.wireOp",EDGE,"E26")])],"isStart":false})],"blendedInto":[makeQuery(id+"F1.opExtrude","CAP_FACE",FACE,{"disambiguationData":[OSD([sQuery(id+"F0.wireOp",EDGE,"E0.rect.bottom"),sQuery(id+"F0.wireOp",EDGE,"E0.rect.top"),sQuery(id+"F0.wireOp",EDGE,"E0.rect.left"),sQuery(id+"F0.wireOp",EDGE,"E0.rect.right"),sQuery(id+"F0.wireOp",EDGE,"E1.left"),sQuery(id+"F0.wireOp",EDGE,"E2.bottom"),sQuery(id+"F0.wireOp",EDGE,"E2.left"),subQ0,subQ1,sQuery(id+"F0.wireOp",EDGE,"E4.bottom"),sQuery(id+"F0.wireOp",EDGE,"E4.left"),sQuery(id+"F0.wireOp",EDGE,"E5"),sQuery(id+"F0.wireOp",EDGE,"E6"),sQuery(id+"F0.wireOp",EDGE,"E7"),sQuery(id+"F0.wireOp",EDGE,"E8"),sQuery(id+"F0.wireOp",EDGE,"E9"),sQuery(id+"F0.wireOp",EDGE,"E10.top"),sQuery(id+"F0.wireOp",EDGE,"E10.left"),sQuery(id+"F0.wireOp",EDGE,"E10.right"),sQuery(id+"F0.wireOp",EDGE,"E11.left"),sQuery(id+"F0.wireOp",EDGE,"E11.right"),sQuery(id+"F0.wireOp",EDGE,"E12.trimOffspring"),sQuery(id+"F0.wireOp",EDGE,"E11.top"),sQuery(id+"F0.wireOp",EDGE,"E15.top"),sQuery(id+"F0.wireOp",EDGE,"E15.left"),sQuery(id+"F0.wireOp",EDGE,"E15.right"),sQuery(id+"F0.wireOp",EDGE,"E16.top"),sQuery(id+"F0.wireOp",EDGE,"E13.right"),sQuery(id+"F0.wireOp",EDGE,"E16.right"),sQuery(id+"F0.wireOp",EDGE,"E17"),sQuery(id+"F0.wireOp",EDGE,"E18.left"),sQuery(id+"F0.wireOp",EDGE,"E18.right"),sQuery(id+"F0.wireOp",EDGE,"E19.left"),sQuery(id+"F0.wireOp",EDGE,"E19.right"),sQuery(id+"F0.wireOp",EDGE,"E20.top"),sQuery(id+"F0.wireOp",EDGE,"E20.left"),sQuery(id+"F0.wireOp",EDGE,"E20.right"),sQuery(id+"F0.wireOp",EDGE,"E21.trimOffspring"),sQuery(id+"F0.wireOp",EDGE,"E22.trimOffspring"),sQuery(id+"F0.wireOp",EDGE,"54661143-fa5e-42c1-9d10-70f3552f3fbd"),sQuery(id+"F0.wireOp",EDGE,"E24"),sQuery(id+"F0.wireOp",EDGE,"E25"),sQuery(id+"F0.wireOp",EDGE,"E26")])],"isStart":false})]});}
            var Q6;
            Q6=makeQuery(id+"F1.opExtrude","CAP_EDGE",EDGE,{"disambiguationData":[OSD([sQuery(id+"F0.wireOp",EDGE,"E0.rect.top"),sQuery(id+"F0.wireOp",EDGE,"E2.bottom"),sQuery(id+"F0.wireOp",EDGE,"E3.bottom")])],"isStart":false});
            var Q7;
            {var subQ0=sQuery(id+"F0.wireOp",EDGE,"E2.bottom");var subQ1=sQuery(id+"F0.wireOp",EDGE,"E2.left");Q7=makeQuery(id+"F2.opFillet","BLEND_EDGE",EDGE,{"blendedFrom":[makeQuery(id+"F1.opExtrude","SWEPT_EDGE",EDGE,{"disambiguationData":[OSD([subQ0,subQ1])]}),makeQuery(id+"F1.opExtrude","CAP_FACE",FACE,{"disambiguationData":[OSD([sQuery(id+"F0.wireOp",EDGE,"E0.rect.bottom"),sQuery(id+"F0.wireOp",EDGE,"E0.rect.top"),sQuery(id+"F0.wireOp",EDGE,"E0.rect.left"),sQuery(id+"F0.wireOp",EDGE,"E0.rect.right"),sQuery(id+"F0.wireOp",EDGE,"E1.left"),subQ0,subQ1,sQuery(id+"F0.wireOp",EDGE,"E3.bottom"),sQuery(id+"F0.wireOp",EDGE,"E3.left"),sQuery(id+"F0.wireOp",EDGE,"E4.bottom"),sQuery(id+"F0.wireOp",EDGE,"E4.left"),sQuery(id+"F0.wireOp",EDGE,"E5"),sQuery(id+"F0.wireOp",EDGE,"E6"),sQuery(id+"F0.wireOp",EDGE,"E7"),sQuery(id+"F0.wireOp",EDGE,"E8"),sQuery(id+"F0.wireOp",EDGE,"E9"),sQuery(id+"F0.wireOp",EDGE,"E10.top"),sQuery(id+"F0.wireOp",EDGE,"E10.left"),sQuery(id+"F0.wireOp",EDGE,"E10.right"),sQuery(id+"F0.wireOp",EDGE,"E11.left"),sQuery(id+"F0.wireOp",EDGE,"E11.right"),sQuery(id+"F0.wireOp",EDGE,"E12.trimOffspring"),sQuery(id+"F0.wireOp",EDGE,"E11.top"),sQuery(id+"F0.wireOp",EDGE,"E15.top"),sQuery(id+"F0.wireOp",EDGE,"E15.left"),sQuery(id+"F0.wireOp",EDGE,"E15.right"),sQuery(id+"F0.wireOp",EDGE,"E16.top"),sQuery(id+"F0.wireOp",EDGE,"E13.right"),sQuery(id+"F0.wireOp",EDGE,"E16.right"),sQuery(id+"F0.wireOp",EDGE,"E17"),sQuery(id+"F0.wireOp",EDGE,"E18.left"),sQuery(id+"F0.wireOp",EDGE,"E18.right"),sQuery(id+"F0.wireOp",EDGE,"E19.left"),sQuery(id+"F0.wireOp",EDGE,"E19.right"),sQuery(id+"F0.wireOp",EDGE,"E20.top"),sQuery(id+"F0.wireOp",EDGE,"E20.left"),sQuery(id+"F0.wireOp",EDGE,"E20.right"),sQuery(id+"F0.wireOp",EDGE,"E21.trimOffspring"),sQuery(id+"F0.wireOp",EDGE,"E22.trimOffspring"),sQuery(id+"F0.wireOp",EDGE,"54661143-fa5e-42c1-9d10-70f3552f3fbd"),sQuery(id+"F0.wireOp",EDGE,"E24"),sQuery(id+"F0.wireOp",EDGE,"E25"),sQuery(id+"F0.wireOp",EDGE,"E26")])],"isStart":false})],"blendedInto":[makeQuery(id+"F1.opExtrude","CAP_FACE",FACE,{"disambiguationData":[OSD([sQuery(id+"F0.wireOp",EDGE,"E0.rect.bottom"),sQuery(id+"F0.wireOp",EDGE,"E0.rect.top"),sQuery(id+"F0.wireOp",EDGE,"E0.rect.left"),sQuery(id+"F0.wireOp",EDGE,"E0.rect.right"),sQuery(id+"F0.wireOp",EDGE,"E1.left"),subQ0,subQ1,sQuery(id+"F0.wireOp",EDGE,"E3.bottom"),sQuery(id+"F0.wireOp",EDGE,"E3.left"),sQuery(id+"F0.wireOp",EDGE,"E4.bottom"),sQuery(id+"F0.wireOp",EDGE,"E4.left"),sQuery(id+"F0.wireOp",EDGE,"E5"),sQuery(id+"F0.wireOp",EDGE,"E6"),sQuery(id+"F0.wireOp",EDGE,"E7"),sQuery(id+"F0.wireOp",EDGE,"E8"),sQuery(id+"F0.wireOp",EDGE,"E9"),sQuery(id+"F0.wireOp",EDGE,"E10.top"),sQuery(id+"F0.wireOp",EDGE,"E10.left"),sQuery(id+"F0.wireOp",EDGE,"E10.right"),sQuery(id+"F0.wireOp",EDGE,"E11.left"),sQuery(id+"F0.wireOp",EDGE,"E11.right"),sQuery(id+"F0.wireOp",EDGE,"E12.trimOffspring"),sQuery(id+"F0.wireOp",EDGE,"E11.top"),sQuery(id+"F0.wireOp",EDGE,"E15.top"),sQuery(id+"F0.wireOp",EDGE,"E15.left"),sQuery(id+"F0.wireOp",EDGE,"E15.right"),sQuery(id+"F0.wireOp",EDGE,"E16.top"),sQuery(id+"F0.wireOp",EDGE,"E13.right"),sQuery(id+"F0.wireOp",EDGE,"E16.right"),sQuery(id+"F0.wireOp",EDGE,"E17"),sQuery(id+"F0.wireOp",EDGE,"E18.left"),sQuery(id+"F0.wireOp",EDGE,"E18.right"),sQuery(id+"F0.wireOp",EDGE,"E19.left"),sQuery(id+"F0.wireOp",EDGE,"E19.right"),sQuery(id+"F0.wireOp",EDGE,"E20.top"),sQuery(id+"F0.wireOp",EDGE,"E20.left"),sQuery(id+"F0.wireOp",EDGE,"E20.right"),sQuery(id+"F0.wireOp",EDGE,"E21.trimOffspring"),sQuery(id+"F0.wireOp",EDGE,"E22.trimOffspring"),sQuery(id+"F0.wireOp",EDGE,"54661143-fa5e-42c1-9d10-70f3552f3fbd"),sQuery(id+"F0.wireOp",EDGE,"E24"),sQuery(id+"F0.wireOp",EDGE,"E25"),sQuery(id+"F0.wireOp",EDGE,"E26")])],"isStart":false})]});}
            var Q8;
            Q8=makeQuery(id+"F1.opExtrude","CAP_EDGE",EDGE,{"disambiguationData":[OSD([sQuery(id+"F0.wireOp",EDGE,"E6")])],"isStart":false});
            var Q9;
            Q9=makeQuery(id+"F1.opExtrude","CAP_EDGE",EDGE,{"disambiguationData":[OSD([sQuery(id+"F0.wireOp",EDGE,"E7")])],"isStart":false});
            var Q10;
            Q10=makeQuery(id+"F1.opExtrude","CAP_EDGE",EDGE,{"disambiguationData":[OSD([sQuery(id+"F0.wireOp",EDGE,"E5")])],"isStart":false});
            var Q11;
            Q11=makeQuery(id+"F1.opExtrude","CAP_EDGE",EDGE,{"disambiguationData":[OSD([sQuery(id+"F0.wireOp",EDGE,"E8")])],"isStart":false});
            var Q12;
            Q12=makeQuery(id+"F1.opExtrude","CAP_EDGE",EDGE,{"disambiguationData":[OSD([sQuery(id+"F0.wireOp",EDGE,"E15.top")])],"isStart":false});
            var Q13;
            Q13=makeQuery(id+"F1.opExtrude","CAP_EDGE",EDGE,{"disambiguationData":[OSD([sQuery(id+"F0.wireOp",EDGE,"E15.right"),sQuery(id+"F0.wireOp",EDGE,"E18.left")])],"isStart":false});
            var Q14;
            Q14=makeQuery(id+"F1.opExtrude","CAP_EDGE",EDGE,{"disambiguationData":[OSD([sQuery(id+"F0.wireOp",EDGE,"E11.right"),sQuery(id+"F0.wireOp",EDGE,"E15.left")])],"isStart":false});
            var Q15;
            Q15=makeQuery(id+"F1.opExtrude","CAP_EDGE",EDGE,{"disambiguationData":[OSD([sQuery(id+"F0.wireOp",EDGE,"E12.trimOffspring")])],"isStart":false});
            var Q16;
            Q16=makeQuery(id+"F1.opExtrude","CAP_EDGE",EDGE,{"disambiguationData":[OSD([sQuery(id+"F0.wireOp",EDGE,"E10.right")])],"isStart":false});
            var Q17;
            Q17=makeQuery(id+"F1.opExtrude","CAP_EDGE",EDGE,{"disambiguationData":[OSD([sQuery(id+"F0.wireOp",EDGE,"E9"),sQuery(id+"F0.wireOp",EDGE,"E21.trimOffspring"),sQuery(id+"F0.wireOp",EDGE,"E22.trimOffspring"),sQuery(id+"F0.wireOp",EDGE,"E25"),sQuery(id+"F0.wireOp",EDGE,"E26")])],"isStart":false});
            var Q18;
            Q18=makeQuery(id+"F1.opExtrude","CAP_EDGE",EDGE,{"disambiguationData":[OSD([sQuery(id+"F0.wireOp",EDGE,"E10.left")])],"isStart":false});
            var Q19;
            Q19=makeQuery(id+"F1.opExtrude","CAP_EDGE",EDGE,{"disambiguationData":[OSD([sQuery(id+"F0.wireOp",EDGE,"E10.top")])],"isStart":false});
            var Q20;
            Q20=makeQuery(id+"F1.opExtrude","CAP_EDGE",EDGE,{"disambiguationData":[OSD([sQuery(id+"F0.wireOp",EDGE,"E11.left")])],"isStart":false});
            var Q21;
            Q21=makeQuery(id+"F1.opExtrude","CAP_EDGE",EDGE,{"disambiguationData":[OSD([sQuery(id+"F0.wireOp",EDGE,"E11.top")])],"isStart":false});
            var Q22;
            Q22=makeQuery(id+"F1.opExtrude","CAP_EDGE",EDGE,{"disambiguationData":[OSD([sQuery(id+"F0.wireOp",EDGE,"E13.right")])],"isStart":false});
            var Q23;
            Q23=makeQuery(id+"F1.opExtrude","CAP_EDGE",EDGE,{"disambiguationData":[OSD([sQuery(id+"F0.wireOp",EDGE,"E16.top")])],"isStart":false});
            var Q24;
            Q24=makeQuery(id+"F1.opExtrude","CAP_EDGE",EDGE,{"disambiguationData":[OSD([sQuery(id+"F0.wireOp",EDGE,"E16.right"),sQuery(id+"F0.wireOp",EDGE,"E19.left")])],"isStart":false});
            var Q25;
            Q25=makeQuery(id+"F1.opExtrude","CAP_EDGE",EDGE,{"disambiguationData":[OSD([sQuery(id+"F0.wireOp",EDGE,"54661143-fa5e-42c1-9d10-70f3552f3fbd")])],"isStart":false});
            var Q26;
            Q26=makeQuery(id+"F1.opExtrude","CAP_EDGE",EDGE,{"disambiguationData":[OSD([sQuery(id+"F0.wireOp",EDGE,"E19.right"),sQuery(id+"F0.wireOp",EDGE,"E20.left")])],"isStart":false});
            var Q27;
            Q27=makeQuery(id+"F1.opExtrude","CAP_EDGE",EDGE,{"disambiguationData":[OSD([sQuery(id+"F0.wireOp",EDGE,"E20.top")])],"isStart":false});
            var Q28;
            Q28=makeQuery(id+"F1.opExtrude","CAP_EDGE",EDGE,{"disambiguationData":[OSD([sQuery(id+"F0.wireOp",EDGE,"E18.right"),sQuery(id+"F0.wireOp",EDGE,"E20.right")])],"isStart":false});
            var Q29;
            Q29=makeQuery(id+"F1.opExtrude","CAP_EDGE",EDGE,{"disambiguationData":[OSD([sQuery(id+"F0.wireOp",EDGE,"E24")])],"isStart":false});
            chamfer(context, id + "F6", {"entities" : qUnion([Q0, Q1, Q2, Q3, Q4, Q5, Q6, Q7, Q8, Q9, Q10, Q11, Q12, Q13, Q14, Q15, Q16, Q17, Q18, Q19, Q20, Q21, Q22, Q23, Q24, Q25, Q26, Q27, Q28, Q29]), "width" : .4 * mm, "tangentPropagation" : true});
        }
        {
            var Q0;
            Q0=makeQuery(id+"F1.opExtrude","CAP_FACE",FACE,{"disambiguationData":[OSD([sQuery(id+"F0.wireOp",EDGE,"E0.rect.bottom"),sQuery(id+"F0.wireOp",EDGE,"E0.rect.top"),sQuery(id+"F0.wireOp",EDGE,"E0.rect.left"),sQuery(id+"F0.wireOp",EDGE,"E0.rect.right"),sQuery(id+"F0.wireOp",EDGE,"E1.left"),sQuery(id+"F0.wireOp",EDGE,"E2.bottom"),sQuery(id+"F0.wireOp",EDGE,"E2.left"),sQuery(id+"F0.wireOp",EDGE,"E3.bottom"),sQuery(id+"F0.wireOp",EDGE,"E3.left"),sQuery(id+"F0.wireOp",EDGE,"E4.bottom"),sQuery(id+"F0.wireOp",EDGE,"E4.left"),sQuery(id+"F0.wireOp",EDGE,"E5"),sQuery(id+"F0.wireOp",EDGE,"E6"),sQuery(id+"F0.wireOp",EDGE,"E7"),sQuery(id+"F0.wireOp",EDGE,"E8"),sQuery(id+"F0.wireOp",EDGE,"E9"),sQuery(id+"F0.wireOp",EDGE,"E10.top"),sQuery(id+"F0.wireOp",EDGE,"E10.left"),sQuery(id+"F0.wireOp",EDGE,"E10.right"),sQuery(id+"F0.wireOp",EDGE,"E11.left"),sQuery(id+"F0.wireOp",EDGE,"E11.right"),sQuery(id+"F0.wireOp",EDGE,"E12.trimOffspring"),sQuery(id+"F0.wireOp",EDGE,"E11.top"),sQuery(id+"F0.wireOp",EDGE,"E15.top"),sQuery(id+"F0.wireOp",EDGE,"E15.left"),sQuery(id+"F0.wireOp",EDGE,"E15.right"),sQuery(id+"F0.wireOp",EDGE,"E16.top"),sQuery(id+"F0.wireOp",EDGE,"E13.right"),sQuery(id+"F0.wireOp",EDGE,"E16.right"),sQuery(id+"F0.wireOp",EDGE,"E17"),sQuery(id+"F0.wireOp",EDGE,"E18.left"),sQuery(id+"F0.wireOp",EDGE,"E18.right"),sQuery(id+"F0.wireOp",EDGE,"E19.left"),sQuery(id+"F0.wireOp",EDGE,"E19.right"),sQuery(id+"F0.wireOp",EDGE,"E20.top"),sQuery(id+"F0.wireOp",EDGE,"E20.left"),sQuery(id+"F0.wireOp",EDGE,"E20.right"),sQuery(id+"F0.wireOp",EDGE,"E21.trimOffspring"),sQuery(id+"F0.wireOp",EDGE,"E22.trimOffspring"),sQuery(id+"F0.wireOp",EDGE,"54661143-fa5e-42c1-9d10-70f3552f3fbd"),sQuery(id+"F0.wireOp",EDGE,"E24"),sQuery(id+"F0.wireOp",EDGE,"E25"),sQuery(id+"F0.wireOp",EDGE,"E26")])],"isStart":true});
            chamfer(context, id + "F7", {"entities" : qUnion([Q0]), "width" : .4 * mm, "tangentPropagation" : true});
        }
        {
            var Q0;
            Q0=makeQuery(id+"F1.opExtrude","SWEPT_BODY",BODY,{"disambiguationData":[OSD([sQuery(id+"F0.wireOp",EDGE,"E0.rect.bottom"),sQuery(id+"F0.wireOp",EDGE,"E0.rect.top"),sQuery(id+"F0.wireOp",EDGE,"E0.rect.left"),sQuery(id+"F0.wireOp",EDGE,"E0.rect.right"),sQuery(id+"F0.wireOp",EDGE,"E1.left"),sQuery(id+"F0.wireOp",EDGE,"E2.bottom"),sQuery(id+"F0.wireOp",EDGE,"E2.left"),sQuery(id+"F0.wireOp",EDGE,"E3.bottom"),sQuery(id+"F0.wireOp",EDGE,"E3.left"),sQuery(id+"F0.wireOp",EDGE,"E4.bottom"),sQuery(id+"F0.wireOp",EDGE,"E4.left"),sQuery(id+"F0.wireOp",EDGE,"E5"),sQuery(id+"F0.wireOp",EDGE,"E6"),sQuery(id+"F0.wireOp",EDGE,"E7"),sQuery(id+"F0.wireOp",EDGE,"E8"),sQuery(id+"F0.wireOp",EDGE,"E9"),sQuery(id+"F0.wireOp",EDGE,"E10.top"),sQuery(id+"F0.wireOp",EDGE,"E10.left"),sQuery(id+"F0.wireOp",EDGE,"E10.right"),sQuery(id+"F0.wireOp",EDGE,"E11.left"),sQuery(id+"F0.wireOp",EDGE,"E11.right"),sQuery(id+"F0.wireOp",EDGE,"E12.trimOffspring"),sQuery(id+"F0.wireOp",EDGE,"E11.top"),sQuery(id+"F0.wireOp",EDGE,"E15.top"),sQuery(id+"F0.wireOp",EDGE,"E15.left"),sQuery(id+"F0.wireOp",EDGE,"E15.right"),sQuery(id+"F0.wireOp",EDGE,"E16.top"),sQuery(id+"F0.wireOp",EDGE,"E13.right"),sQuery(id+"F0.wireOp",EDGE,"E16.right"),sQuery(id+"F0.wireOp",EDGE,"E17"),sQuery(id+"F0.wireOp",EDGE,"E18.left"),sQuery(id+"F0.wireOp",EDGE,"E18.right"),sQuery(id+"F0.wireOp",EDGE,"E19.left"),sQuery(id+"F0.wireOp",EDGE,"E19.right"),sQuery(id+"F0.wireOp",EDGE,"E20.top"),sQuery(id+"F0.wireOp",EDGE,"E20.left"),sQuery(id+"F0.wireOp",EDGE,"E20.right"),sQuery(id+"F0.wireOp",EDGE,"E21.trimOffspring"),sQuery(id+"F0.wireOp",EDGE,"E22.trimOffspring"),sQuery(id+"F0.wireOp",EDGE,"54661143-fa5e-42c1-9d10-70f3552f3fbd"),sQuery(id+"F0.wireOp",EDGE,"E24"),sQuery(id+"F0.wireOp",EDGE,"E25"),sQuery(id+"F0.wireOp",EDGE,"E26")])]});
            var Q1;
            {var subQ0=sQuery(id+"F0.wireOp",EDGE,"E0.rect.top");var subQ1=sQuery(id+"F0.wireOp",EDGE,"E2.bottom");var subQ2=sQuery(id+"F0.wireOp",EDGE,"E3.bottom");Q1=makeQuery(id+"F7.opChamfer","BLEND_EDGE",EDGE,{"blendedFrom":[makeQuery(id+"F1.opExtrude","CAP_EDGE",EDGE,{"disambiguationData":[OSD([subQ0,subQ1,subQ2])],"isStart":true}),makeQuery(id+"F1.opExtrude","SWEPT_FACE",FACE,{"disambiguationData":[OSD([subQ0,subQ1,subQ2])]})],"blendedInto":[makeQuery(id+"F1.opExtrude","SWEPT_FACE",FACE,{"disambiguationData":[OSD([subQ0,subQ1,subQ2])]})]});}
            transform(context, id + "F8", {"entities" : qUnion([Q0]), "transformType" : TransformType.ROTATION, "transformAxis" : qUnion([Q1]), "angle" : 180 * degree, "makeCopy" : false});
        }
    });
